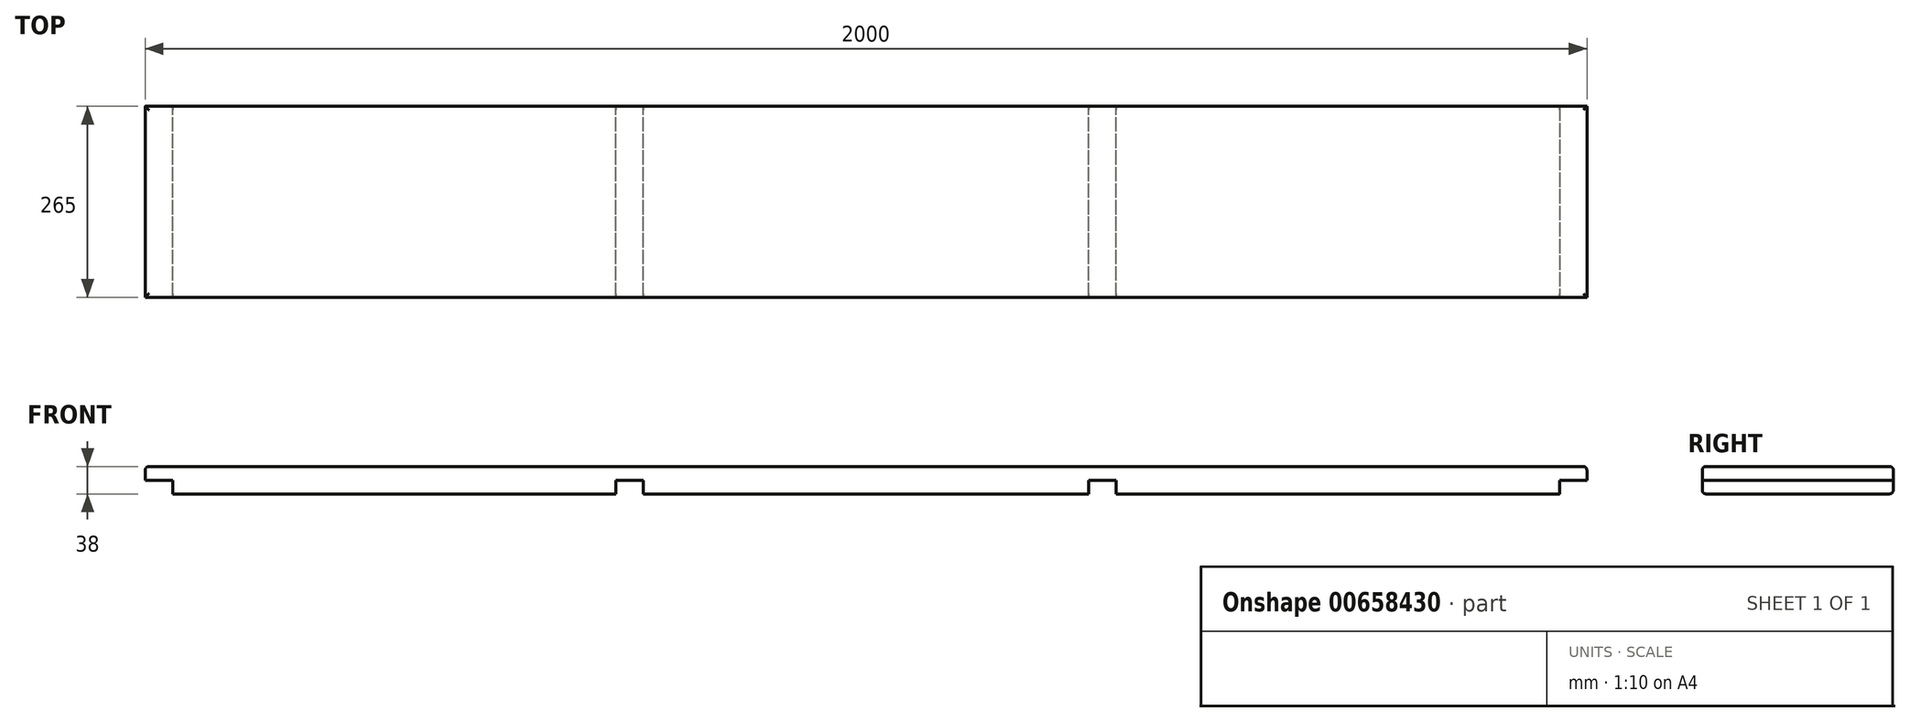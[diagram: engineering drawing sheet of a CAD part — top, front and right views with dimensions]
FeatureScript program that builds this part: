
annotation { "Feature Type Name" : "Feature", "Feature Type Description" : "" }
export const myFeature = defineFeature(function(context is Context, id is Id, definition is map)
    precondition{}
    {
        {
            var Q0;
            Q0=qCreatedBy(makeId("Top.planeOp"),FACE);
            var sketch = newSketch(context, id + "F0", { "sketchPlane" : qUnion([Q0])});
            skLineSegment(sketch, "E0.bottom", {"start": v(-997.38, -246.9) * mm, "end": v(1002.62, -246.9) * mm});
            skLineSegment(sketch, "E0.top", {"start": v(-997.38, -511.9) * mm, "end": v(1002.62, -511.9) * mm});
            skLineSegment(sketch, "E0.left", {"start": v(-997.38, -246.9) * mm, "end": v(-997.38, -511.9) * mm});
            skLineSegment(sketch, "E0.right", {"start": v(1002.62, -246.9) * mm, "end": v(1002.62, -511.9) * mm});
            skSolve(sketch);
        }
        {
            var Q0;
            Q0 = qSketchRegion(id + "F0", true);
            extrude(context, id + "F1", {"entities" : qUnion([Q0]), "depth" : 38 * mm, "offsetDistance" : 25 * mm});
        }
        {
            var Q0;
            Q0=makeQuery(id+"F1.opExtrude","CAP_FACE",FACE,{"disambiguationData":[OSD([sQuery(id+"F0.wireOp",EDGE,"E0.bottom"),sQuery(id+"F0.wireOp",EDGE,"E0.top"),sQuery(id+"F0.wireOp",EDGE,"E0.left"),sQuery(id+"F0.wireOp",EDGE,"E0.right")])],"isStart":false});
            var Q1;
            Q1=makeQuery(id+"F1.opExtrude","CAP_FACE",FACE,{"disambiguationData":[OSD([sQuery(id+"F0.wireOp",EDGE,"E0.bottom"),sQuery(id+"F0.wireOp",EDGE,"E0.top"),sQuery(id+"F0.wireOp",EDGE,"E0.left"),sQuery(id+"F0.wireOp",EDGE,"E0.right")])],"isStart":true});
            fillet(context, id + "F2", {"entities" : qUnion([Q0, Q1]), "radius" : 5 * mm, "tangentPropagation" : true, "allowEdgeOverflow" : false});
        }
        {
            var Q0;
            Q0=makeQuery(id+"F1.opExtrude","CAP_FACE",FACE,{"disambiguationData":[OSD([sQuery(id+"F0.wireOp",EDGE,"E0.bottom"),sQuery(id+"F0.wireOp",EDGE,"E0.top"),sQuery(id+"F0.wireOp",EDGE,"E0.left"),sQuery(id+"F0.wireOp",EDGE,"E0.right")])],"isStart":true});
            var sketch = newSketch(context, id + "F3", { "sketchPlane" : qUnion([Q0])});
            skLineSegment(sketch, "E1.bottom", {"start": v(-1004.2, 574.66) * mm, "end": v(-959.38, 574.66) * mm});
            skLineSegment(sketch, "E1.top", {"start": v(-1004.2, 193.99) * mm, "end": v(-959.38, 193.99) * mm});
            skLineSegment(sketch, "E1.left", {"start": v(-1004.2, 574.66) * mm, "end": v(-1004.2, 193.99) * mm});
            skLineSegment(sketch, "E1.right", {"start": v(-959.38, 574.66) * mm, "end": v(-959.38, 193.99) * mm});
            skLineSegment(sketch, "E2.bottom", {"start": v(1035.4, 204.24) * mm, "end": v(964.62, 204.24) * mm});
            skLineSegment(sketch, "E2.top", {"start": v(1035.4, 568.49) * mm, "end": v(964.62, 568.49) * mm});
            skLineSegment(sketch, "E2.left", {"start": v(1035.4, 204.24) * mm, "end": v(1035.4, 568.49) * mm});
            skLineSegment(sketch, "E2.right", {"start": v(964.62, 204.24) * mm, "end": v(964.62, 568.49) * mm});
            skSolve(sketch);
        }
        {
            var Q0;
            Q0 = qSketchRegion(id + "F3", true);
            extrude(context, id + "F4", {"entities" : qUnion([Q0]), "operationType" : NewBodyOperationType.REMOVE, "oppositeDirection" : true, "depth" : 19 * mm, "offsetDistance" : 25 * mm});
        }
        {
            var Q0;
            Q0=makeQuery(id+"F1.opExtrude","CAP_FACE",FACE,{"disambiguationData":[OSD([sQuery(id+"F0.wireOp",EDGE,"E0.bottom"),sQuery(id+"F0.wireOp",EDGE,"E0.top"),sQuery(id+"F0.wireOp",EDGE,"E0.left"),sQuery(id+"F0.wireOp",EDGE,"E0.right")])],"isStart":true});
            var sketch = newSketch(context, id + "F5", { "sketchPlane" : qUnion([Q0])});
            skLineSegment(sketch, "E3.bottom", {"start": v(-344.38, 524.87) * mm, "end": v(-306.38, 524.87) * mm});
            skLineSegment(sketch, "E3.top", {"start": v(-344.38, 182.06) * mm, "end": v(-306.38, 182.06) * mm});
            skLineSegment(sketch, "E3.left", {"start": v(-344.38, 524.87) * mm, "end": v(-344.38, 182.06) * mm});
            skLineSegment(sketch, "E3.right", {"start": v(-306.38, 524.87) * mm, "end": v(-306.38, 182.06) * mm});
            skLineSegment(sketch, "E4.bottom", {"start": v(311.62, 572.95) * mm, "end": v(349.62, 572.95) * mm});
            skLineSegment(sketch, "E4.top", {"start": v(311.62, 138.4) * mm, "end": v(349.62, 138.4) * mm});
            skLineSegment(sketch, "E4.left", {"start": v(311.62, 572.95) * mm, "end": v(311.62, 138.4) * mm});
            skLineSegment(sketch, "E4.right", {"start": v(349.62, 572.95) * mm, "end": v(349.62, 138.4) * mm});
            skSolve(sketch);
        }
        {
            var Q0;
            Q0 = qSketchRegion(id + "F5", true);
            extrude(context, id + "F6", {"entities" : qUnion([Q0]), "operationType" : NewBodyOperationType.REMOVE, "oppositeDirection" : true, "depth" : 19 * mm, "offsetDistance" : 25 * mm});
        }
    });
